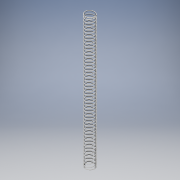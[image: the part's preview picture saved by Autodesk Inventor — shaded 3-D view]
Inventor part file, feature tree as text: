
AUTODESK INVENTOR PART (.ipt)
format: ipt  version: 2018 (Build 220112000, 112)  size: 1,435,648 bytes
history: native  units: in
note: dims shown in document units (in); Inventor stores cm internally (conversion verified against a paired STEP export)
features: helix x1, sketch x1
ambient origin geometry x8: Origin, YZ Plane, XZ Plane, XY Plane, X Axis, Y Axis, Z Axis, Center Point
bodies: Solid1 (feature_tree)
feature tree (2):
  helix  "Coil1"  [1 undecoded]
  sketch  "Sketch1"  dims[d1=0.47in d2=1.0in d3=12.5in d4=17.3228in d5=0.0in d6=90.0deg d7=1.3056in d8=90.0deg d9=1.3056in]
note: 1 required parameter value undecoded (feature->parameter linkage not recoverable at this tier; creation-order binding heuristic only, values carry confidence <= 0.55)
